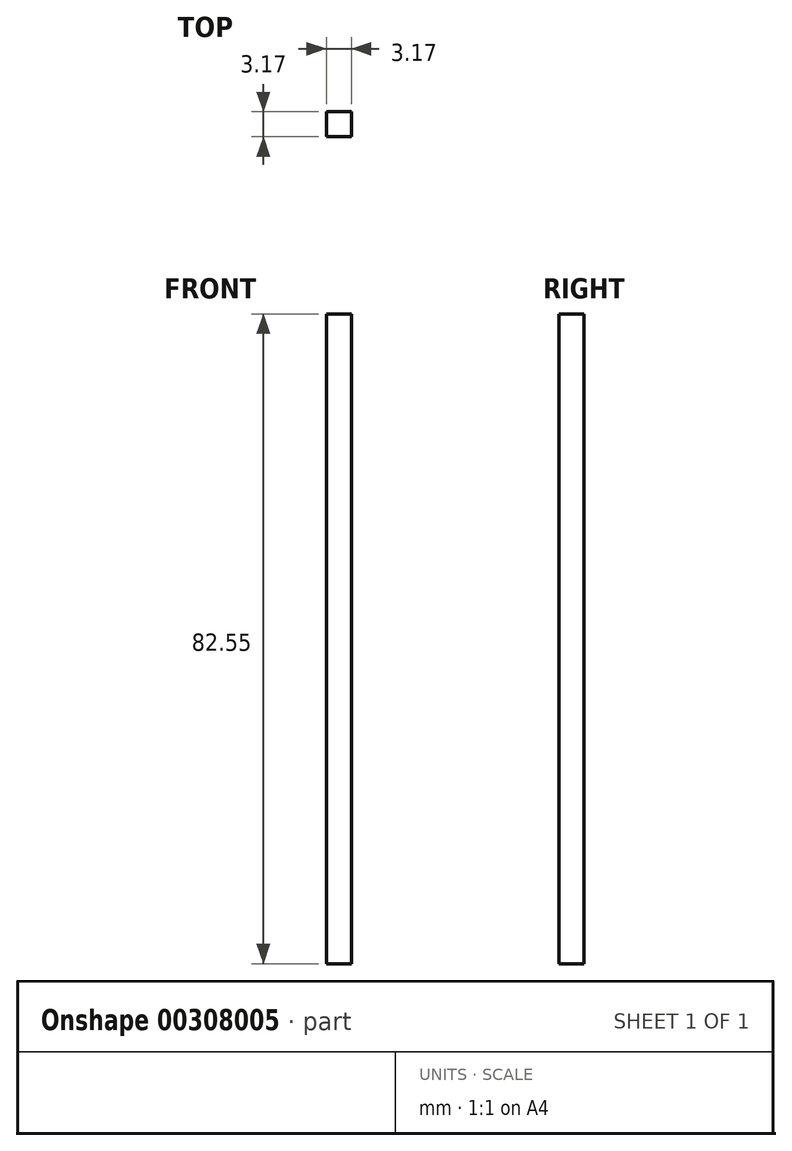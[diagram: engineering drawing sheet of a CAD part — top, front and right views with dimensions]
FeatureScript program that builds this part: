
annotation { "Feature Type Name" : "Feature", "Feature Type Description" : "" }
export const myFeature = defineFeature(function(context is Context, id is Id, definition is map)
    precondition{}
    {
        {
            var Q0;
            Q0=qCreatedBy(makeId("Right.planeOp"),FACE);
            var sketch = newSketch(context, id + "F0", { "sketchPlane" : qUnion([Q0])});
            skLineSegment(sketch, "E0.bottom", {"start": v(0, 0) * mm, "end": v(3.18, 0) * mm});
            skLineSegment(sketch, "E0.top", {"start": v(0, 82.55) * mm, "end": v(3.17, 82.55) * mm});
            skLineSegment(sketch, "E0.left", {"start": v(0, 0) * mm, "end": v(0, 82.55) * mm});
            skLineSegment(sketch, "E0.right", {"start": v(3.18, 0) * mm, "end": v(3.17, 82.55) * mm});
            skSolve(sketch);
        }
        {
            var Q0;
            {var subQ1=sQuery(id+"F0.wireOp",EDGE,"E0.bottom");Q0=makeQuery(id+"F0.imprint","IMPRINT",FACE,{"disambiguationData":[TD([[makeQuery(id+"F0.imprint","IMPRINT",EDGE,{"derivedFrom":subQ1}),1.0]])]});}
            var Q1;
            {var subQ1=sQuery(id+"F0.wireOp",EDGE,"UHRCmWCn-Ting-mLDZ-D4Dz-jSR8Vt5UYdtT");Q1=makeQuery(id+"F0.imprint","IMPRINT",FACE,{"disambiguationData":[TD([[makeQuery(id+"F0.imprint","IMPRINT",EDGE,{"derivedFrom":subQ1}),-1.0]])]});}
            extrude(context, id + "F1", {"entities" : qUnion([Q0, Q1]), "depth" : 3.17 * mm});
        }
    });
